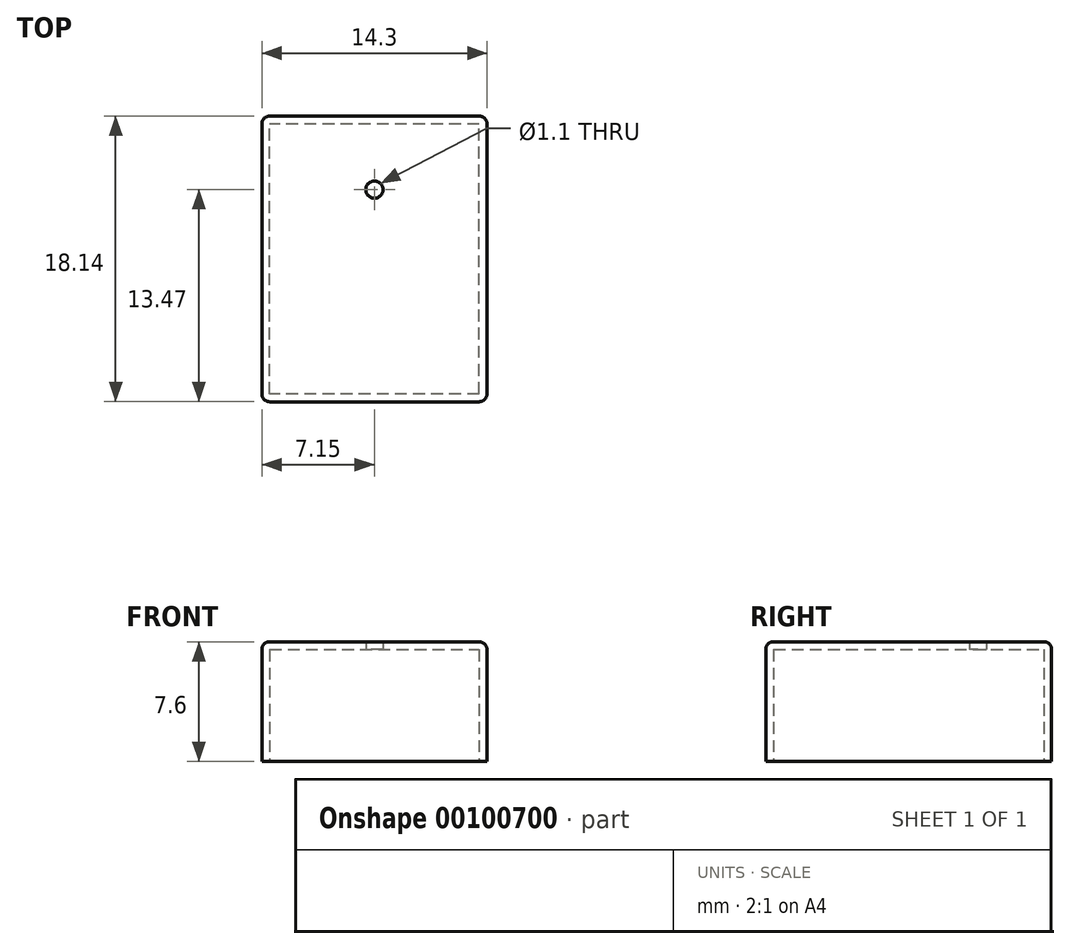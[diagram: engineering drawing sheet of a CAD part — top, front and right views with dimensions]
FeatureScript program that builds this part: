
annotation { "Feature Type Name" : "Feature", "Feature Type Description" : "" }
export const myFeature = defineFeature(function(context is Context, id is Id, definition is map)
    precondition{}
    {
        {
            var Q0;
            Q0=qCreatedBy(makeId("Top.planeOp"),FACE);
            var sketch = newSketch(context, id + "F3", { "sketchPlane" : qUnion([Q0])});
            skLineSegment(sketch, "E0.bottom", {"start": v(7.15, -9.07) * mm, "end": v(-7.15, -9.07) * mm});
            skLineSegment(sketch, "E0.top", {"start": v(7.15, 9.08) * mm, "end": v(-7.15, 9.07) * mm});
            skLineSegment(sketch, "E0.left", {"start": v(7.15, -9.07) * mm, "end": v(7.15, 9.07) * mm});
            skLineSegment(sketch, "E0.right", {"start": v(-7.15, -9.07) * mm, "end": v(-7.15, 9.07) * mm});
            skPoint(sketch, "E0.middle", {"position": v(0, 0) * mm});
            skSolve(sketch);
        }
        {
            var Q0;
            Q0 = qSketchRegion(id + "F3", true);
            extrude(context, id + "F4", {"entities" : qUnion([Q0]), "depth" : 7.6 * mm});
        }
        {
            var Q0;
            Q0=makeQuery(id+"F4.opExtrude","SWEPT_EDGE",EDGE,{"disambiguationData":[OSD([sQuery(id+"F3.wireOp",EDGE,"E0.bottom"),sQuery(id+"F3.wireOp",EDGE,"E0.right")])]});
            var Q1;
            Q1=makeQuery(id+"F4.opExtrude","SWEPT_EDGE",EDGE,{"disambiguationData":[OSD([sQuery(id+"F3.wireOp",EDGE,"E0.bottom"),sQuery(id+"F3.wireOp",EDGE,"E0.left")])]});
            var Q2;
            Q2=makeQuery(id+"F4.opExtrude","CAP_EDGE",EDGE,{"disambiguationData":[OSD([sQuery(id+"F3.wireOp",EDGE,"E0.left")])],"isStart":false});
            var Q3;
            Q3=makeQuery(id+"F4.opExtrude","SWEPT_EDGE",EDGE,{"disambiguationData":[OSD([sQuery(id+"F3.wireOp",EDGE,"E0.top"),sQuery(id+"F3.wireOp",EDGE,"E0.right")])]});
            var Q4;
            Q4=makeQuery(id+"F4.opExtrude","SWEPT_EDGE",EDGE,{"disambiguationData":[OSD([sQuery(id+"F3.wireOp",EDGE,"E0.top"),sQuery(id+"F3.wireOp",EDGE,"E0.left")])]});
            var Q5;
            Q5=makeQuery(id+"F4.opExtrude","CAP_EDGE",EDGE,{"disambiguationData":[OSD([sQuery(id+"F3.wireOp",EDGE,"E0.right")])],"isStart":false});
            var Q6;
            Q6=makeQuery(id+"F4.opExtrude","CAP_EDGE",EDGE,{"disambiguationData":[OSD([sQuery(id+"F3.wireOp",EDGE,"E0.top")])],"isStart":false});
            var Q7;
            Q7=makeQuery(id+"F4.opExtrude","CAP_EDGE",EDGE,{"disambiguationData":[OSD([sQuery(id+"F3.wireOp",EDGE,"E0.bottom")])],"isStart":false});
            fillet(context, id + "F5", {"entities" : qUnion([Q0, Q1, Q2, Q3, Q4, Q5, Q6, Q7]), "radius" : 0.5 * mm, "tangentPropagation" : true, "allowEdgeOverflow" : false});
        }
        {
            var Q0;
            Q0=makeQuery(id+"F4.opExtrude","CAP_FACE",FACE,{"disambiguationData":[OSD([sQuery(id+"F3.wireOp",EDGE,"E0.bottom"),sQuery(id+"F3.wireOp",EDGE,"E0.top"),sQuery(id+"F3.wireOp",EDGE,"E0.left"),sQuery(id+"F3.wireOp",EDGE,"E0.right")])],"isStart":true});
            shell(context, id + "F0", {"entities" : qUnion([Q0]), "thickness" : 0.5 * mm});
        }
        {
            var Q0;
            Q0=makeQuery(id+"F4.opExtrude","CAP_FACE",FACE,{"disambiguationData":[OSD([sQuery(id+"F3.wireOp",EDGE,"E0.bottom"),sQuery(id+"F3.wireOp",EDGE,"E0.top"),sQuery(id+"F3.wireOp",EDGE,"E0.left"),sQuery(id+"F3.wireOp",EDGE,"E0.right")])],"isStart":false});
            var sketch = newSketch(context, id + "F1", { "sketchPlane" : qUnion([Q0])});
            skLineSegment(sketch, "E1", {"start": v(0, 0) * mm, "end": v(0, 4.4) * mm, "construction": true});
            skPoint(sketch, "E2", {"position": v(0, 4.4) * mm});
            skSolve(sketch);
        }
        {
            var Q0;
            Q0=sQuery(id+"F1.wireOp",VERTEX,"E2");
            var Q1;
            Q1=makeQuery(id+"F4.opExtrude","SWEPT_BODY",BODY,{"disambiguationData":[OSD([sQuery(id+"F3.wireOp",EDGE,"E0.bottom"),sQuery(id+"F3.wireOp",EDGE,"E0.top"),sQuery(id+"F3.wireOp",EDGE,"E0.left"),sQuery(id+"F3.wireOp",EDGE,"E0.right")])]});
            hole(context, id + "F2", {"style" : HoleStyle.SIMPLE, "endStyle" : HoleEndStyle.THROUGH, "holeDiameter" : 1.1 * mm, "locations" : qUnion([Q0]), "scope" : qUnion([Q1]), "isTappedThrough" : true, "startStyle" : HoleStartStyle.PART});
        }
    });
